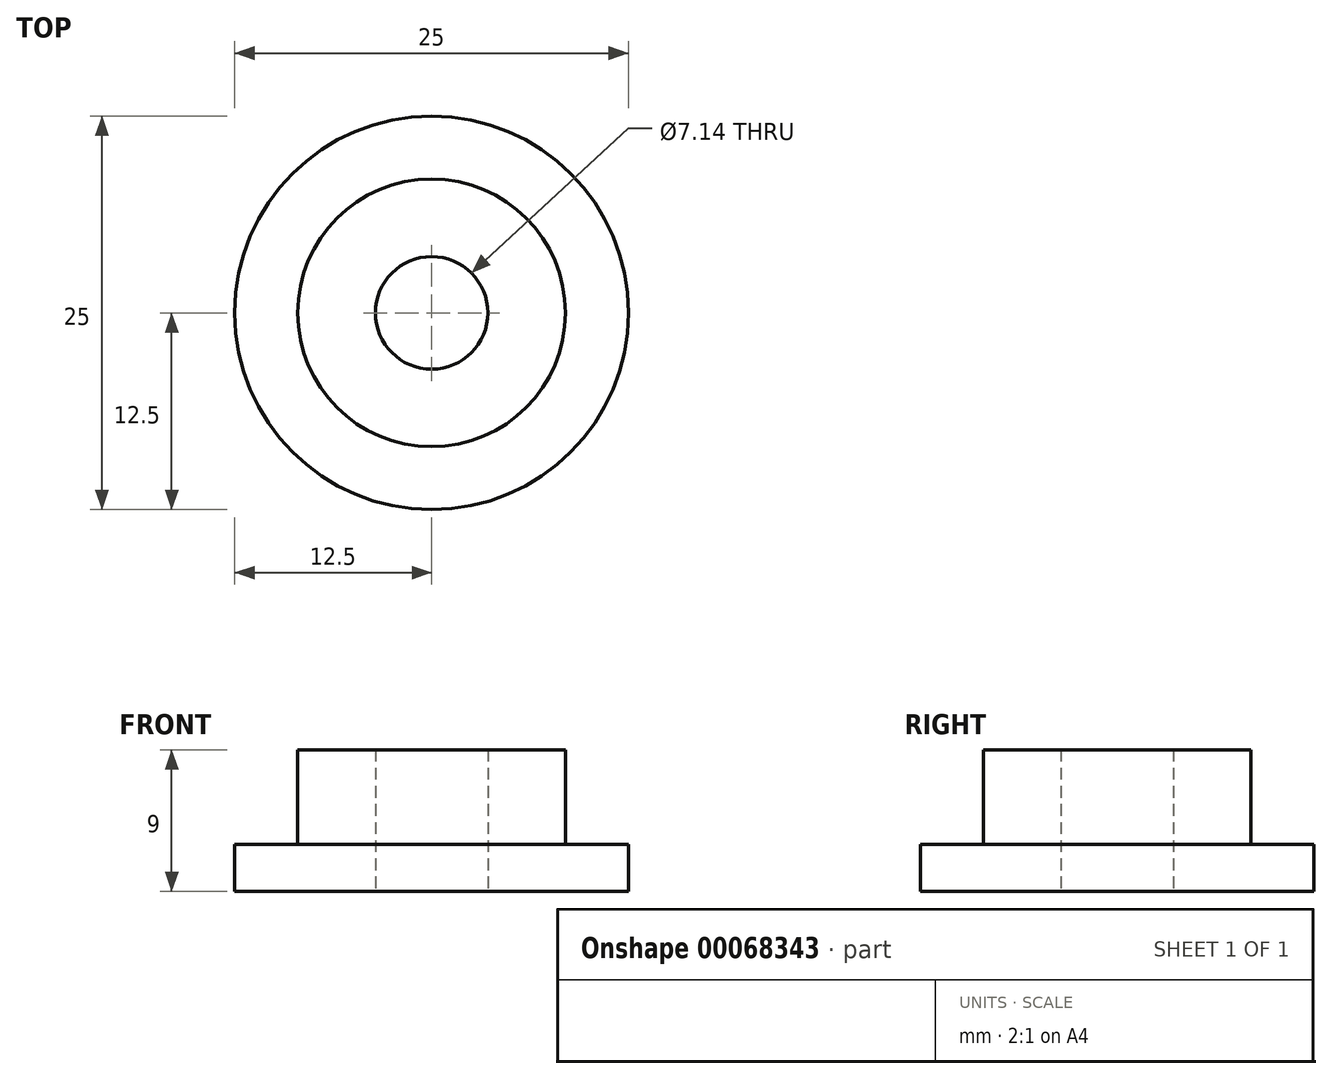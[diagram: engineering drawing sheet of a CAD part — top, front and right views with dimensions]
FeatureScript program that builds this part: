
annotation { "Feature Type Name" : "Feature", "Feature Type Description" : "" }
export const myFeature = defineFeature(function(context is Context, id is Id, definition is map)
    precondition{}
    {
        {
            var Q0;
            Q0=qCreatedBy(makeId("Top.planeOp"),FACE);
            var sketch = newSketch(context, id + "F0", { "sketchPlane" : qUnion([Q0])});
            skCircle(sketch, "E0", {"center": v(0, 0) * mm, "radius": 12.5 * mm});
            skCircle(sketch, "E1", {"center": v(0, 0) * mm, "radius": 8.5 * mm});
            skCircle(sketch, "E2", {"center": v(0, 0) * mm, "radius": 3.57 * mm});
            skSolve(sketch);
        }
        {
            var Q0;
            Q0=makeQuery(id+"F0.imprint","IMPRINT",FACE,{"disambiguationData":[TD([[makeQuery(id+"F0.imprint","IMPRINT",EDGE,{"derivedFrom":sQuery(id+"F0.wireOp",EDGE,"E0")}),1.0]])]});
            extrude(context, id + "F1", {"entities" : qUnion([Q0]), "depth" : 3 * mm});
        }
        {
            var Q0;
            Q0=makeQuery(id+"F0.imprint","IMPRINT",FACE,{"disambiguationData":[TD([[makeQuery(id+"F0.imprint","IMPRINT",EDGE,{"derivedFrom":sQuery(id+"F0.wireOp",EDGE,"E1")}),1.0]])]});
            extrude(context, id + "F2", {"entities" : qUnion([Q0]), "operationType" : NewBodyOperationType.ADD, "depth" : (6 + 3) * mm});
        }
    });
